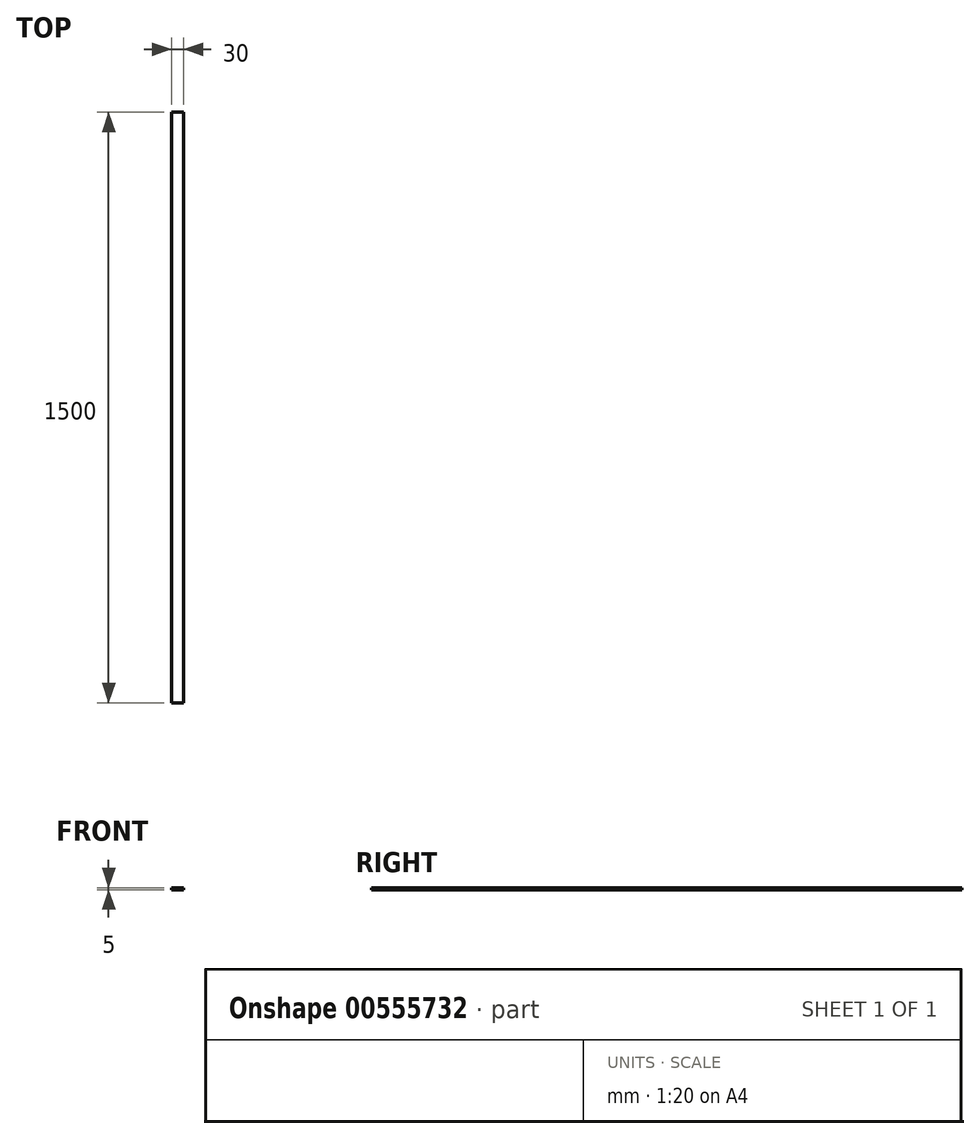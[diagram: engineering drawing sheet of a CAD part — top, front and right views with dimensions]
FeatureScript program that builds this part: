
annotation { "Feature Type Name" : "Feature", "Feature Type Description" : "" }
export const myFeature = defineFeature(function(context is Context, id is Id, definition is map)
    precondition{}
    {
        {
            var Q0;
            Q0=qCreatedBy(makeId("Top.planeOp"),FACE);
            var sketch = newSketch(context, id + "F0", { "sketchPlane" : qUnion([Q0])});
            skLineSegment(sketch, "E0.bottom", {"start": v(15, 750) * mm, "end": v(-15, 750) * mm});
            skLineSegment(sketch, "E0.top", {"start": v(15, -750) * mm, "end": v(-15, -750) * mm});
            skLineSegment(sketch, "E0.left", {"start": v(15, 750) * mm, "end": v(15, -750) * mm});
            skLineSegment(sketch, "E0.right", {"start": v(-15, 750) * mm, "end": v(-15, -750) * mm});
            skPoint(sketch, "E0.middle", {"position": v(0, 0) * mm});
            skSolve(sketch);
        }
        {
            var Q0;
            Q0=makeQuery(id+"F0.imprint","IMPRINT",FACE,{"disambiguationData":[TD([[makeQuery(id+"F0.imprint","IMPRINT",EDGE,{"derivedFrom":sQuery(id+"F0.wireOp",EDGE,"E0.bottom")}),1.0]])]});
            extrude(context, id + "F1", {"entities" : qUnion([Q0]), "depth" : 5 * mm, "offsetDistance" : 25 * mm});
        }
    });
